# Revit family: TYCO-FPP-Zettler-RIM800 Relay interface module
name_source: partatom
category: Electrical Fixtures
revit_build: Autodesk Revit 2014 (Build: 20130308_1515(x64)
units: mm (PartAtom-declared; Revit-internal decimal feet)

## types (1)
- TYCO-FPP-Zettler-RIM800 Relay interface module
    Ambient Temperature = –25°C to +70°C
    Description = The RIM800 Addressable Relay Interface Module provides one volt-free changeover contact output unsupervised.
    Front cover = Yes
    Keynote = The RIM800 is supplied as an open circuit board (PCB) with mounting hardware and must be fitted in a suitable enclosure.
    Length = 61 mm
    Loop Voltage = 20V to 40Vdc
    Manufacturer = Tyco
    Max. RIM800 per Loop4 = 200/250
    Model = Zettler - 568.800.003
    Operating Humidity = 10% to 95% non condensing
    PCB = PCB
    Quiescent Current = 285μA
    Rear cover = Yes
    Standby current = 2.8mA
    Storage Temperature = –40°C to +80°C
    Type Comments = The RIM800 has a red LED which may be configured to indicate relay activation and c.i.e. polling.
    URL = http://www.zettlerfire.com
    Width = 84 mm
    Wire Size = Min 2.5mm2

## geometry (parser evidence)
native form markers: Sweep x3
no freeform markers — native parametric forms only
